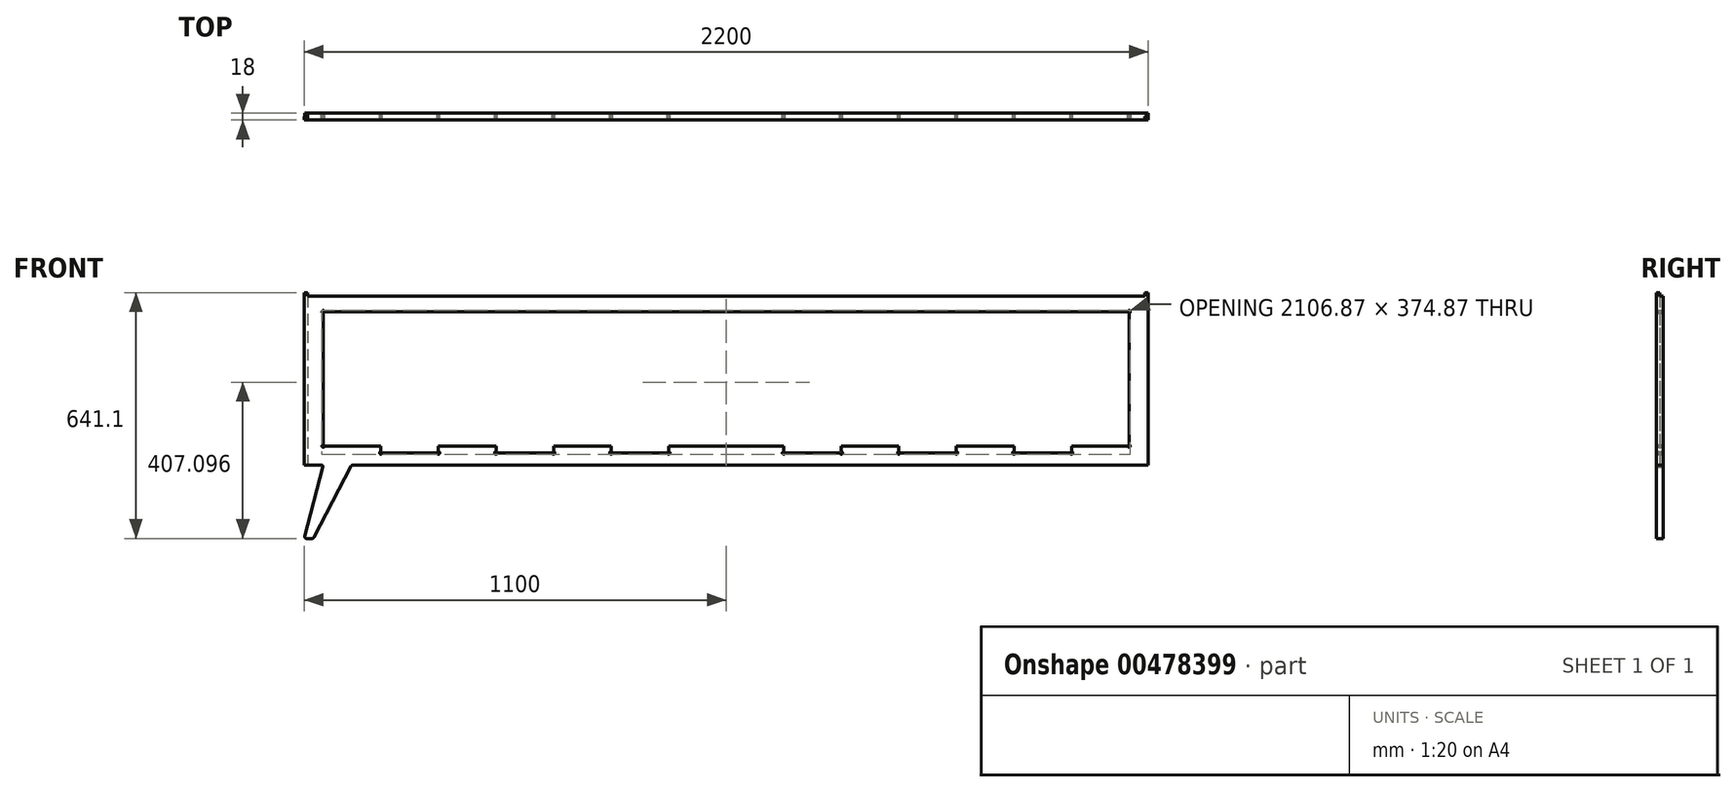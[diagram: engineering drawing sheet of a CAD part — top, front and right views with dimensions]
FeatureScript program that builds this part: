
annotation { "Feature Type Name" : "Feature", "Feature Type Description" : "" }
export const myFeature = defineFeature(function(context is Context, id is Id, definition is map)
    precondition{}
    {
        {
            var Q0;
            Q0=qCreatedBy(makeId("Front.planeOp"),FACE);
            var sketch = newSketch(context, id + "F0", { "sketchPlane" : qUnion([Q0])});
            skLineSegment(sketch, "E0.bottom", {"start": v(-1100, 75.88) * mm, "end": v(0, 75.88) * mm});
            skLineSegment(sketch, "E0.top", {"start": v(-1100, -374.12) * mm, "end": v(-1055, -374.12) * mm});
            skLineSegment(sketch, "E0.left", {"start": v(-1100, 75.88) * mm, "end": v(-1100, -374.12) * mm});
            skLineSegment(sketch, "E0.right", {"start": v(0, 25.88) * mm, "end": v(0, -324.12) * mm, "construction": true});
            skLineSegment(sketch, "E1", {"start": v(-1100, -374.12) * mm, "end": v(-1100, -565.22) * mm, "construction": true});
            skLineSegment(sketch, "E2", {"start": v(-1050, -374.12) * mm, "end": v(-1050, -374.12) * mm});
            skLineSegment(sketch, "E3", {"start": v(-1093.52, -565.22) * mm, "end": v(-1078.8, -565.22) * mm});
            skLineSegment(sketch, "E4", {"start": v(-1074.37, -562.53) * mm, "end": v(-977.78, -376.82) * mm});
            skPoint(sketch, "E5.visualSharp", {"position": v(-1100, -565.22) * mm});
            skArc(sketch, "E5.filletArc", {"start": v(-1098.36, -558.95) * mm, "mid": v(-1097.48, -563.28) * mm, "end": v(-1093.52, -565.22) * mm});
            skPoint(sketch, "E6.visualSharp", {"position": v(-1075.77, -565.22) * mm});
            skArc(sketch, "E6.filletArc", {"start": v(-1078.8, -565.22) * mm, "mid": v(-1076.21, -564.5) * mm, "end": v(-1074.37, -562.53) * mm});
            skLineSegment(sketch, "E7", {"start": v(-973.35, -374.12) * mm, "end": v(0, -374.12) * mm});
            skPoint(sketch, "E8.visualSharp", {"position": v(-976.38, -374.12) * mm});
            skArc(sketch, "E8.filletArc", {"start": v(-973.35, -374.12) * mm, "mid": v(-975.94, -374.85) * mm, "end": v(-977.78, -376.82) * mm});
            skArc(sketch, "E9", {"start": v(-1051.27, -378.96) * mm, "mid": v(-1051.86, -375.56) * mm, "end": v(-1055, -374.12) * mm});
            skLineSegment(sketch, "E10", {"start": v(-1051.27, -378.96) * mm, "end": v(-1098.36, -558.95) * mm});
            skLineSegment(sketch, "E11", {"start": v(-1050, 22.38) * mm, "end": v(-1050, -320.62) * mm});
            skLineSegment(sketch, "E12", {"start": v(-1046.5, 25.88) * mm, "end": v(0, 25.88) * mm});
            skArc(sketch, "E13.MirrorCS", {"start": v(1078.8, -565.22) * mm, "mid": v(1076.21, -564.5) * mm, "end": v(1074.37, -562.53) * mm});
            skLineSegment(sketch, "E14.MirrorCS", {"start": v(1093.52, -565.22) * mm, "end": v(1078.8, -565.22) * mm});
            skArc(sketch, "E15.MirrorCS", {"start": v(1098.36, -558.95) * mm, "mid": v(1097.48, -563.28) * mm, "end": v(1093.52, -565.22) * mm});
            skArc(sketch, "E16.MirrorCS", {"start": v(973.35, -374.12) * mm, "mid": v(975.94, -374.85) * mm, "end": v(977.78, -376.82) * mm});
            skArc(sketch, "E17.MirrorCS", {"start": v(1051.27, -378.96) * mm, "mid": v(1051.86, -375.56) * mm, "end": v(1055, -374.12) * mm});
            skPoint(sketch, "E18.MirrorP", {"position": v(1100, -565.22) * mm});
            skPoint(sketch, "E19.MirrorP", {"position": v(976.38, -374.12) * mm});
            skLineSegment(sketch, "E20.MirrorCS", {"start": v(1050, -374.12) * mm, "end": v(1050, -374.12) * mm});
            skLineSegment(sketch, "E21.MirrorCS", {"start": v(1074.37, -562.53) * mm, "end": v(977.78, -376.82) * mm});
            skLineSegment(sketch, "E22.MirrorCS", {"start": v(1100, 75.88) * mm, "end": v(1100, -374.12) * mm});
            skPoint(sketch, "E23.MirrorP", {"position": v(1075.77, -565.22) * mm});
            skLineSegment(sketch, "E24.MirrorCS", {"start": v(1100, -374.12) * mm, "end": v(1055, -374.12) * mm});
            skLineSegment(sketch, "E25.MirrorCS", {"start": v(1100, -374.12) * mm, "end": v(1100, -565.22) * mm, "construction": true});
            skLineSegment(sketch, "E26.MirrorCS", {"start": v(1051.27, -378.96) * mm, "end": v(1098.36, -558.95) * mm});
            skLineSegment(sketch, "E27.MirrorCS", {"start": v(1050.19, 25.88) * mm, "end": v(1050, 25.88) * mm});
            skLineSegment(sketch, "E28.MirrorCS", {"start": v(1100, 75.88) * mm, "end": v(0, 75.88) * mm});
            skLineSegment(sketch, "E29.MirrorCS", {"start": v(973.35, -374.12) * mm, "end": v(0, -374.12) * mm});
            skPoint(sketch, "E30", {"position": v(0, 75.88) * mm});
            skPoint(sketch, "E31", {"position": v(0, 25.88) * mm});
            skLineSegment(sketch, "E32.bottom", {"start": v(-1046.5, 25.88) * mm, "end": v(1046.5, 25.88) * mm});
            skLineSegment(sketch, "E32.top", {"start": v(-1046.5, -324.12) * mm, "end": v(-900, -324.12) * mm});
            skPoint(sketch, "E33", {"position": v(-1100, 75.88) * mm});
            skLineSegment(sketch, "E34.0", {"start": v(-1100, 66.88) * mm, "end": v(0, 66.88) * mm});
            skLineSegment(sketch, "E35.0", {"start": v(-1091, 75.88) * mm, "end": v(-1091, -374.12) * mm});
            skLineSegment(sketch, "E36.MirrorCS", {"start": v(1100, 66.88) * mm, "end": v(0, 66.88) * mm});
            skLineSegment(sketch, "E37.MirrorCS", {"start": v(1091, 75.88) * mm, "end": v(1091, -374.12) * mm});
            skLineSegment(sketch, "E38", {"start": v(-1055, -374.12) * mm, "end": v(-973.35, -374.12) * mm});
            skLineSegment(sketch, "E39.MirrorCS", {"start": v(1055, -374.12) * mm, "end": v(973.35, -374.12) * mm});
            skLineSegment(sketch, "E40", {"start": v(1091, -365.04) * mm, "end": v(1091, -365.12) * mm});
            skPoint(sketch, "E41.end.orphan", {"position": v(1091, -374.12) * mm});
            skPoint(sketch, "E42.orphan", {"position": v(1100, -365.12) * mm});
            skLineSegment(sketch, "E43", {"start": v(1055, -374.12) * mm, "end": v(1055, -326.71) * mm, "construction": true});
            skLineSegment(sketch, "E44", {"start": v(973.35, -374.12) * mm, "end": v(973.35, -365.12) * mm, "construction": true});
            skLineSegment(sketch, "E45", {"start": v(-900, -324.12) * mm, "end": v(-900, -338.62) * mm});
            skLineSegment(sketch, "E46", {"start": v(-896.5, -342.12) * mm, "end": v(-753.5, -342.12) * mm});
            skLineSegment(sketch, "E47", {"start": v(-750, -338.62) * mm, "end": v(-750, -324.12) * mm});
            skArc(sketch, "E48", {"start": v(-1050, -320.62) * mm, "mid": v(-1052.47, -326.6) * mm, "end": v(-1046.5, -324.12) * mm});
            skArc(sketch, "E49", {"start": v(-900, -338.62) * mm, "mid": v(-902.47, -344.6) * mm, "end": v(-896.5, -342.12) * mm});
            skArc(sketch, "E50", {"start": v(-750, -338.62) * mm, "mid": v(-747.53, -344.6) * mm, "end": v(-753.5, -342.12) * mm});
            skLineSegment(sketch, "E51", {"start": v(-750, -324.12) * mm, "end": v(-600, -324.12) * mm});
            skLineSegment(sketch, "E52.1.0.0", {"start": v(-600, -324.12) * mm, "end": v(-600, -338.62) * mm});
            skLineSegment(sketch, "E52.1.0.1", {"start": v(-450, -338.62) * mm, "end": v(-450, -324.12) * mm});
            skLineSegment(sketch, "E52.1.0.2", {"start": v(-450, -324.12) * mm, "end": v(-300, -324.12) * mm});
            skLineSegment(sketch, "E52.1.0.3", {"start": v(-596.5, -342.12) * mm, "end": v(-453.5, -342.12) * mm});
            skArc(sketch, "E52.1.0.4", {"start": v(-600, -338.62) * mm, "mid": v(-602.47, -344.6) * mm, "end": v(-596.5, -342.12) * mm});
            skArc(sketch, "E52.1.0.5", {"start": v(-450, -338.62) * mm, "mid": v(-447.53, -344.6) * mm, "end": v(-453.5, -342.12) * mm});
            skLineSegment(sketch, "E52.2.0.0", {"start": v(-300, -324.12) * mm, "end": v(-300, -338.62) * mm});
            skLineSegment(sketch, "E52.2.0.1", {"start": v(-150, -338.62) * mm, "end": v(-150, -324.12) * mm});
            skLineSegment(sketch, "E52.2.0.2", {"start": v(-150, -324.12) * mm, "end": v(0, -324.12) * mm});
            skLineSegment(sketch, "E52.2.0.3", {"start": v(-296.5, -342.12) * mm, "end": v(-153.5, -342.12) * mm});
            skArc(sketch, "E52.2.0.4", {"start": v(-300, -338.62) * mm, "mid": v(-302.47, -344.6) * mm, "end": v(-296.5, -342.12) * mm});
            skArc(sketch, "E52.2.0.5", {"start": v(-150, -338.62) * mm, "mid": v(-147.53, -344.6) * mm, "end": v(-153.5, -342.12) * mm});
            skLineSegment(sketch, "E52.direction1", {"start": v(-900, -342.12) * mm, "end": v(-600, -342.12) * mm, "construction": true});
            skArc(sketch, "E53.MirrorCS", {"start": v(750, -338.62) * mm, "mid": v(747.53, -344.6) * mm, "end": v(753.5, -342.12) * mm});
            skArc(sketch, "E54.MirrorCS", {"start": v(900, -338.62) * mm, "mid": v(902.47, -344.6) * mm, "end": v(896.5, -342.12) * mm});
            skLineSegment(sketch, "E55.MirrorCS", {"start": v(600, -324.12) * mm, "end": v(600, -338.62) * mm});
            skLineSegment(sketch, "E56.MirrorCS", {"start": v(450, -338.62) * mm, "end": v(450, -324.12) * mm});
            skLineSegment(sketch, "E57.MirrorCS", {"start": v(900, -324.12) * mm, "end": v(900, -338.62) * mm});
            skArc(sketch, "E58.MirrorCS", {"start": v(600, -338.62) * mm, "mid": v(602.47, -344.6) * mm, "end": v(596.5, -342.12) * mm});
            skLineSegment(sketch, "E59.MirrorCS", {"start": v(300, -324.12) * mm, "end": v(300, -338.62) * mm});
            skArc(sketch, "E60.MirrorCS", {"start": v(450, -338.62) * mm, "mid": v(447.53, -344.6) * mm, "end": v(453.5, -342.12) * mm});
            skArc(sketch, "E61.MirrorCS", {"start": v(150, -338.62) * mm, "mid": v(147.53, -344.6) * mm, "end": v(153.5, -342.12) * mm});
            skArc(sketch, "E62.MirrorCS", {"start": v(300, -338.62) * mm, "mid": v(302.47, -344.6) * mm, "end": v(296.5, -342.12) * mm});
            skLineSegment(sketch, "E63.MirrorCS", {"start": v(750, -338.62) * mm, "end": v(750, -324.12) * mm});
            skLineSegment(sketch, "E64.MirrorCS", {"start": v(150, -338.62) * mm, "end": v(150, -324.12) * mm});
            skLineSegment(sketch, "E65.MirrorCS", {"start": v(896.5, -342.12) * mm, "end": v(753.5, -342.12) * mm});
            skLineSegment(sketch, "E66.MirrorCS", {"start": v(750, -324.12) * mm, "end": v(600, -324.12) * mm});
            skLineSegment(sketch, "E67.MirrorCS", {"start": v(150, -324.12) * mm, "end": v(0, -324.12) * mm});
            skLineSegment(sketch, "E68.MirrorCS", {"start": v(596.5, -342.12) * mm, "end": v(453.5, -342.12) * mm});
            skLineSegment(sketch, "E69.MirrorCS", {"start": v(296.5, -342.12) * mm, "end": v(153.5, -342.12) * mm});
            skLineSegment(sketch, "E70.MirrorCS", {"start": v(1046.5, -324.12) * mm, "end": v(900, -324.12) * mm});
            skLineSegment(sketch, "E71.MirrorCS", {"start": v(900, -342.12) * mm, "end": v(600, -342.12) * mm, "construction": true});
            skLineSegment(sketch, "E72.MirrorCS", {"start": v(450, -324.12) * mm, "end": v(300, -324.12) * mm});
            skArc(sketch, "E73.MirrorCS", {"start": v(1050, -320.62) * mm, "mid": v(1052.47, -326.6) * mm, "end": v(1046.5, -324.12) * mm});
            skLineSegment(sketch, "E74.MirrorCS", {"start": v(1050, 22.38) * mm, "end": v(1050, -320.62) * mm});
            skArc(sketch, "E75", {"start": v(-1050, 22.38) * mm, "mid": v(-1052.47, 28.35) * mm, "end": v(-1046.5, 25.88) * mm});
            skPoint(sketch, "E76.orphan", {"position": v(-1050.19, 25.88) * mm});
            skArc(sketch, "E77", {"start": v(1050, 22.38) * mm, "mid": v(1052.47, 28.35) * mm, "end": v(1046.5, 25.88) * mm});
            skLineSegment(sketch, "E78.trimOffspring", {"start": v(1046.5, 25.88) * mm, "end": v(0, 25.88) * mm});
            skSolve(sketch);
        }
        {
            var Q0;
            {var subQ0=sQuery(id+"F0.wireOp",EDGE,"E0.left");var subQ1=sQuery(id+"F0.wireOp",EDGE,"E0.bottom");var subQ2=makeQuery(id+"F0.imprint","INTERSECT",VERTEX,{"derivedFrom":[subQ1,subQ0]});Q0=makeQuery(id+"F0.imprint","IMPRINT",FACE,{"disambiguationData":[TD([[makeQuery(id+"F0.imprint","IMPRINT",EDGE,{"disambiguationData":[TD([[subQ2,-1.0]])],"derivedFrom":subQ1}),-1.0]])]});}
            var Q1;
            Q1=makeQuery(id+"F0.imprint","IMPRINT",FACE,{"disambiguationData":[TD([[makeQuery(id+"F0.imprint","IMPRINT",EDGE,{"derivedFrom":sQuery(id+"F0.wireOp",EDGE,"E32.bottom")}),1.0]])]});
            var Q2;
            Q2=makeQuery(id+"F0.imprint","IMPRINT",FACE,{"disambiguationData":[TD([[makeQuery(id+"F0.imprint","IMPRINT",EDGE,{"derivedFrom":sQuery(id+"F0.wireOp",EDGE,"E3")}),1.0]])]});
            var Q3;
            {var subQ0=sQuery(id+"F0.wireOp",EDGE,"E36.MirrorCS");var subQ1=sQuery(id+"F0.wireOp",EDGE,"E22.MirrorCS");var subQ2=makeQuery(id+"F0.imprint","INTERSECT",VERTEX,{"derivedFrom":[subQ1,subQ0]});Q3=makeQuery(id+"F0.imprint","IMPRINT",FACE,{"disambiguationData":[TD([[makeQuery(id+"F0.imprint","IMPRINT",EDGE,{"disambiguationData":[TD([[subQ2,-1.0]])],"derivedFrom":subQ1}),-1.0]])]});}
            var Q4;
            {var subQ1=sQuery(id+"F0.wireOp",EDGE,"E0.bottom");var subQ7=sQuery(id+"F0.wireOp",EDGE,"E28.MirrorCS");var subQ8=makeQuery(id+"F0.imprint","INTERSECT",VERTEX,{"derivedFrom":[subQ1,subQ7]});Q4=makeQuery(id+"F0.imprint","IMPRINT",FACE,{"disambiguationData":[TD([[makeQuery(id+"F0.imprint","IMPRINT",EDGE,{"disambiguationData":[TD([[subQ8,1.0]])],"derivedFrom":subQ1}),-1.0]])]});}
            var Q5;
            {var subQ0=sQuery(id+"F0.wireOp",EDGE,"E34.0");var subQ1=sQuery(id+"F0.wireOp",EDGE,"E0.left");var subQ2=makeQuery(id+"F0.imprint","INTERSECT",VERTEX,{"derivedFrom":[subQ1,subQ0]});Q5=makeQuery(id+"F0.imprint","IMPRINT",FACE,{"disambiguationData":[TD([[makeQuery(id+"F0.imprint","IMPRINT",EDGE,{"disambiguationData":[TD([[subQ2,-1.0]])],"derivedFrom":subQ1}),1.0]])]});}
            var Q6;
            {var subQ0=sQuery(id+"F0.wireOp",EDGE,"E0.left");var subQ1=sQuery(id+"F0.wireOp",EDGE,"E0.top");var subQ2=makeQuery(id+"F0.imprint","INTERSECT",VERTEX,{"derivedFrom":[subQ1,subQ0]});Q6=makeQuery(id+"F0.imprint","IMPRINT",FACE,{"disambiguationData":[TD([[makeQuery(id+"F0.imprint","IMPRINT",EDGE,{"disambiguationData":[TD([[subQ2,-1.0]])],"derivedFrom":subQ1}),1.0]])]});}
            var Q7;
            {var subQ0=sQuery(id+"F0.wireOp",EDGE,"E22.MirrorCS");var subQ1=sQuery(id+"F0.wireOp",EDGE,"E28.MirrorCS");var subQ2=makeQuery(id+"F0.imprint","INTERSECT",VERTEX,{"derivedFrom":[subQ1,subQ0]});Q7=makeQuery(id+"F0.imprint","IMPRINT",FACE,{"disambiguationData":[TD([[makeQuery(id+"F0.imprint","IMPRINT",EDGE,{"disambiguationData":[TD([[subQ2,-1.0]])],"derivedFrom":subQ1}),1.0]])]});}
            var Q8;
            {var subQ0=sQuery(id+"F0.wireOp",EDGE,"E24.MirrorCS");var subQ1=sQuery(id+"F0.wireOp",EDGE,"E22.MirrorCS");var subQ2=makeQuery(id+"F0.imprint","INTERSECT",VERTEX,{"derivedFrom":[subQ1,subQ0]});Q8=makeQuery(id+"F0.imprint","IMPRINT",FACE,{"disambiguationData":[TD([[makeQuery(id+"F0.imprint","IMPRINT",EDGE,{"disambiguationData":[TD([[subQ2,1.0]])],"derivedFrom":subQ1}),-1.0]])]});}
            var Q9;
            Q9=makeQuery(id+"F0.imprint","IMPRINT",FACE,{"disambiguationData":[TD([[makeQuery(id+"F0.imprint","IMPRINT",EDGE,{"derivedFrom":sQuery(id+"F0.wireOp",EDGE,"E13.MirrorCS")}),-1.0]])]});
            extrude(context, id + "F1", {"entities" : qUnion([Q0, Q1, Q2, Q3, Q4, Q5, Q6, Q7, Q8, Q9]), "depth" : 18 * mm});
        }
        {
            var Q0;
            {var subQ5=sQuery(id+"F0.wireOp",EDGE,"E0.bottom");var subQ7=sQuery(id+"F0.wireOp",EDGE,"E28.MirrorCS");var subQ8=makeQuery(id+"F0.imprint","INTERSECT",VERTEX,{"derivedFrom":[subQ5,subQ7]});Q0=makeQuery(id+"F0.imprint","IMPRINT",FACE,{"disambiguationData":[TD([[makeQuery(id+"F0.imprint","IMPRINT",EDGE,{"disambiguationData":[TD([[subQ8,1.0]])],"derivedFrom":subQ5}),-1.0]])]});}
            var Q1;
            {var subQ0=sQuery(id+"F0.wireOp",EDGE,"E22.MirrorCS");var subQ1=sQuery(id+"F0.wireOp",EDGE,"E28.MirrorCS");var subQ2=makeQuery(id+"F0.imprint","INTERSECT",VERTEX,{"derivedFrom":[subQ1,subQ0]});Q1=makeQuery(id+"F0.imprint","IMPRINT",FACE,{"disambiguationData":[TD([[makeQuery(id+"F0.imprint","IMPRINT",EDGE,{"disambiguationData":[TD([[subQ2,-1.0]])],"derivedFrom":subQ1}),1.0]])]});}
            var Q2;
            {var subQ0=sQuery(id+"F0.wireOp",EDGE,"E0.left");var subQ1=sQuery(id+"F0.wireOp",EDGE,"E0.top");var subQ2=makeQuery(id+"F0.imprint","INTERSECT",VERTEX,{"derivedFrom":[subQ1,subQ0]});Q2=makeQuery(id+"F0.imprint","IMPRINT",FACE,{"disambiguationData":[TD([[makeQuery(id+"F0.imprint","IMPRINT",EDGE,{"disambiguationData":[TD([[subQ2,-1.0]])],"derivedFrom":subQ1}),1.0]])]});}
            var Q3;
            {var subQ0=sQuery(id+"F0.wireOp",EDGE,"E0.left");var subQ1=sQuery(id+"F0.wireOp",EDGE,"E0.bottom");var subQ2=makeQuery(id+"F0.imprint","INTERSECT",VERTEX,{"derivedFrom":[subQ1,subQ0]});Q3=makeQuery(id+"F0.imprint","IMPRINT",FACE,{"disambiguationData":[TD([[makeQuery(id+"F0.imprint","IMPRINT",EDGE,{"disambiguationData":[TD([[subQ2,-1.0]])],"derivedFrom":subQ1}),-1.0]])]});}
            var Q4;
            {var subQ0=sQuery(id+"F0.wireOp",EDGE,"E40");Q4=makeQuery(id+"F0.imprint","IMPRINT",FACE,{"disambiguationData":[TD([[makeQuery(id+"F0.imprint","IMPRINT",EDGE,{"derivedFrom":subQ0}),1.0]])]});}
            extrude(context, id + "F2", {"entities" : qUnion([Q0, Q1, Q2, Q3, Q4]), "operationType" : NewBodyOperationType.REMOVE, "oppositeDirection" : true, "depth" : -9 * mm});
        }
    });
